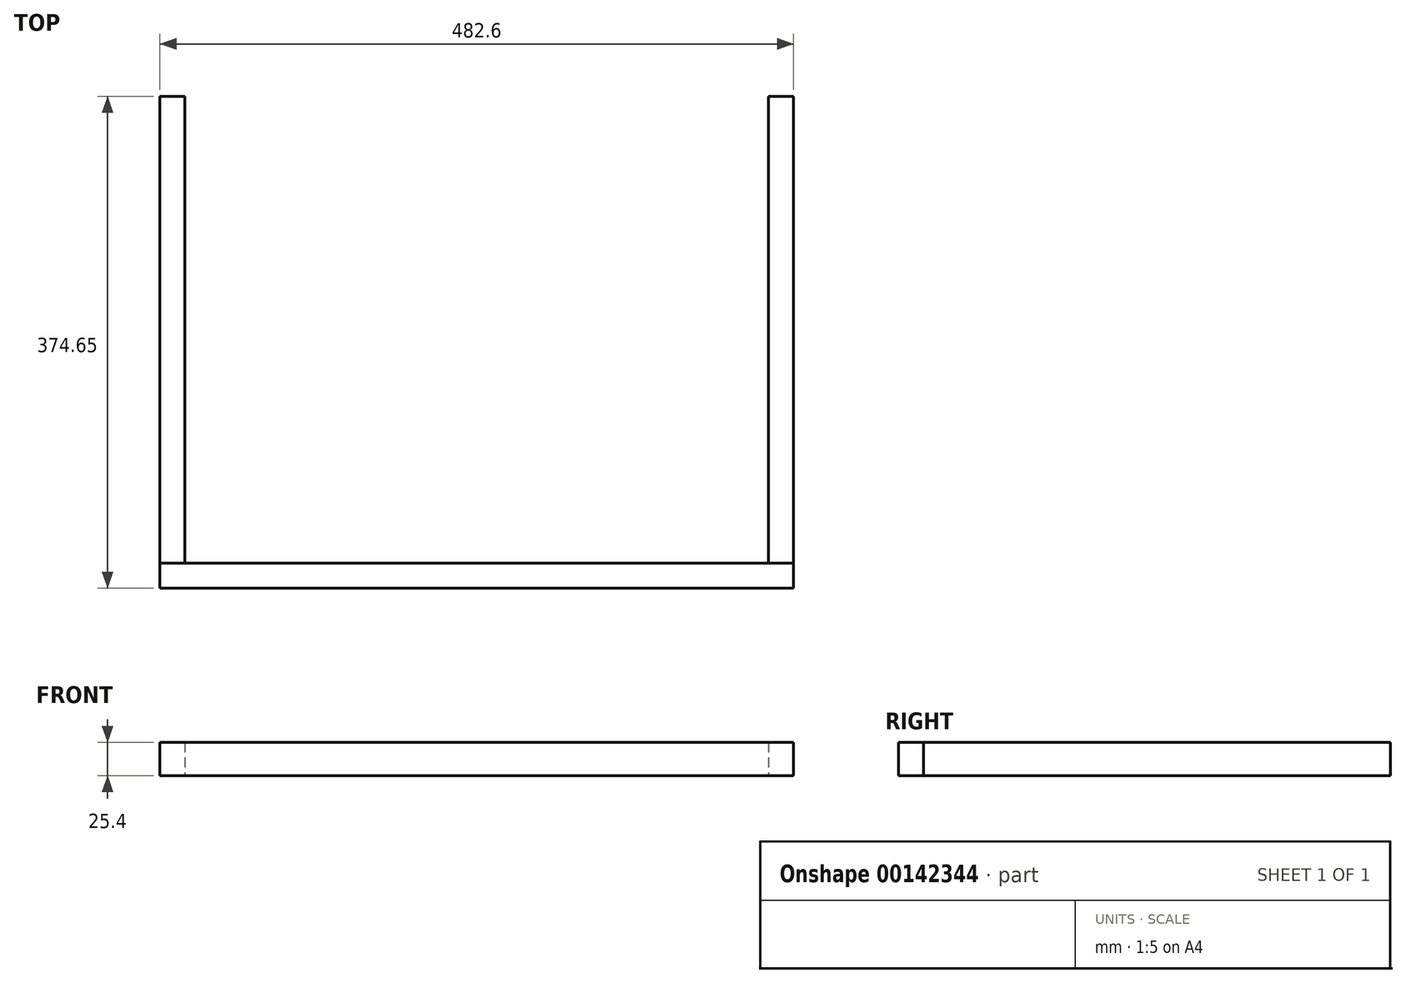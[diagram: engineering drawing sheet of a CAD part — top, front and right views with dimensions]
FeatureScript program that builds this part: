
annotation { "Feature Type Name" : "Feature", "Feature Type Description" : "" }
export const myFeature = defineFeature(function(context is Context, id is Id, definition is map)
    precondition{}
    {
        {
            var Q0;
            Q0=qCreatedBy(makeId("Right.planeOp"),FACE);
            var sketch = newSketch(context, id + "F0", { "sketchPlane" : qUnion([Q0])});
            skLineSegment(sketch, "E0.bottom", {"start": v(10.64, 8.77) * mm, "end": v(-8.41, 8.77) * mm});
            skLineSegment(sketch, "E0.top", {"start": v(10.64, -16.63) * mm, "end": v(-8.41, -16.63) * mm});
            skLineSegment(sketch, "E0.left", {"start": v(10.64, 8.77) * mm, "end": v(10.64, -16.63) * mm});
            skLineSegment(sketch, "E0.right", {"start": v(-8.41, 8.77) * mm, "end": v(-8.41, -16.63) * mm});
            skSolve(sketch);
        }
        {
            var Q0;
            Q0=makeQuery(id+"F0.imprint","IMPRINT",FACE,{"disambiguationData":[TD([[makeQuery(id+"F0.imprint","IMPRINT",EDGE,{"derivedFrom":sQuery(id+"F0.wireOp",EDGE,"E0.bottom")}),1.0]])]});
            extrude(context, id + "F1", {"entities" : qUnion([Q0]), "depth" : 482.6 * mm});
        }
        {
            var Q0;
            Q0=makeQuery(id+"F1.opExtrude","SWEPT_FACE",FACE,{"disambiguationData":[OSD([sQuery(id+"F0.wireOp",EDGE,"E0.left")])]});
            var sketch = newSketch(context, id + "F2", { "sketchPlane" : qUnion([Q0])});
            skLineSegment(sketch, "E1.bottom", {"start": v(0, 8.77) * mm, "end": v(-19.05, 8.77) * mm});
            skLineSegment(sketch, "E1.top", {"start": v(0, -16.63) * mm, "end": v(-19.05, -16.63) * mm});
            skLineSegment(sketch, "E1.left", {"start": v(0, 8.77) * mm, "end": v(0, -16.63) * mm});
            skLineSegment(sketch, "E1.right", {"start": v(-19.05, 8.77) * mm, "end": v(-19.05, -16.63) * mm});
            skSolve(sketch);
        }
        {
            var Q0;
            Q0=makeQuery(id+"F2.imprint","IMPRINT",FACE,{"disambiguationData":[TD([[makeQuery(id+"F2.imprint","IMPRINT",EDGE,{"derivedFrom":sQuery(id+"F2.wireOp",EDGE,"E1.bottom")}),-1.0]])]});
            extrude(context, id + "F3", {"entities" : qUnion([Q0]), "depth" : 355.6 * mm});
        }
        {
            var Q0;
            Q0=makeQuery(id+"F1.opExtrude","SWEPT_FACE",FACE,{"disambiguationData":[OSD([sQuery(id+"F0.wireOp",EDGE,"E0.left")])]});
            var sketch = newSketch(context, id + "F4", { "sketchPlane" : qUnion([Q0])});
            skLineSegment(sketch, "E2.bottom", {"start": v(-482.6, 8.77) * mm, "end": v(-463.55, 8.77) * mm});
            skLineSegment(sketch, "E2.top", {"start": v(-482.6, -16.63) * mm, "end": v(-463.55, -16.63) * mm});
            skLineSegment(sketch, "E2.left", {"start": v(-482.6, 8.77) * mm, "end": v(-482.6, -16.63) * mm});
            skLineSegment(sketch, "E2.right", {"start": v(-463.55, 8.77) * mm, "end": v(-463.55, -16.63) * mm});
            skSolve(sketch);
        }
        {
            var Q0;
            Q0=makeQuery(id+"F4.imprint","IMPRINT",FACE,{"disambiguationData":[TD([[makeQuery(id+"F4.imprint","IMPRINT",EDGE,{"derivedFrom":sQuery(id+"F4.wireOp",EDGE,"E2.bottom")}),-1.0]])]});
            extrude(context, id + "F5", {"entities" : qUnion([Q0]), "depth" : 355.6 * mm});
        }
    });
